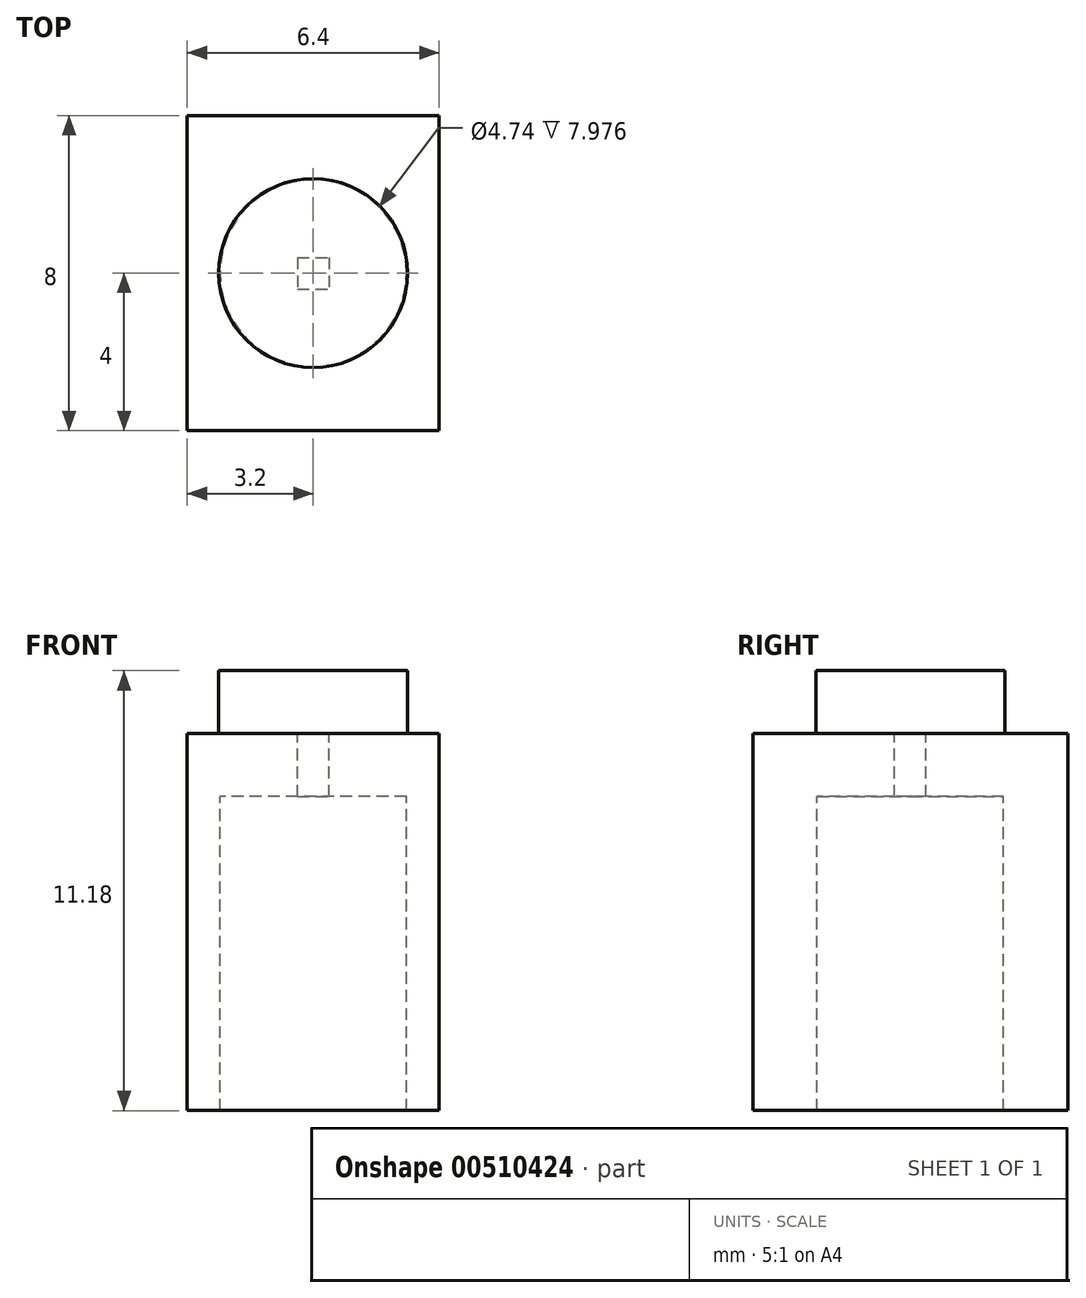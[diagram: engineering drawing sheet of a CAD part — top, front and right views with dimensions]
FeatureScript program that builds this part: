
annotation { "Feature Type Name" : "Feature", "Feature Type Description" : "" }
export const myFeature = defineFeature(function(context is Context, id is Id, definition is map)
    precondition{}
    {
        {
            var Q0;
            Q0=qCreatedBy(makeId("Front.planeOp"),FACE);
            var sketch = newSketch(context, id + "F0", { "sketchPlane" : qUnion([Q0])});
            skLineSegment(sketch, "E0", {"start": v(0, 0) * mm, "end": v(-3.2, 0) * mm});
            skLineSegment(sketch, "E1.MirrorCS", {"start": v(0, 0) * mm, "end": v(3.2, 0) * mm});
            skLineSegment(sketch, "E2", {"start": v(3.2, 0) * mm, "end": v(3.2, -9.58) * mm});
            skLineSegment(sketch, "E3.MirrorCS", {"start": v(-3.2, 0) * mm, "end": v(-3.2, -9.58) * mm});
            skLineSegment(sketch, "E4", {"start": v(-3.2, -9.58) * mm, "end": v(3.2, -9.58) * mm});
            skSolve(sketch);
        }
        {
            var Q0;
            Q0=qCreatedBy(makeId("Top.planeOp"),FACE);
            var sketch = newSketch(context, id + "F1", { "sketchPlane" : qUnion([Q0])});
            skCircle(sketch, "E5", {"center": v(0, 0) * mm, "radius": 2.4 * mm});
            skSolve(sketch);
        }
        {
            var Q0;
            Q0=qCreatedBy(makeId("Top.planeOp"),FACE);
            var sketch = newSketch(context, id + "F2", { "sketchPlane" : qUnion([Q0])});
            skCircle(sketch, "E6", {"center": v(0, 0) * mm, "radius": 2.37 * mm});
            skSolve(sketch);
        }
        {
            var Q0;
            Q0=qCreatedBy(makeId("Top.planeOp"),FACE);
            var sketch = newSketch(context, id + "F3", { "sketchPlane" : qUnion([Q0])});
            skLineSegment(sketch, "E7.bottom", {"start": v(-0.4, 0.4) * mm, "end": v(0.4, 0.4) * mm});
            skLineSegment(sketch, "E7.top", {"start": v(-0.4, -0.4) * mm, "end": v(0.4, -0.4) * mm});
            skLineSegment(sketch, "E7.left", {"start": v(-0.4, 0.4) * mm, "end": v(-0.4, -0.4) * mm});
            skLineSegment(sketch, "E7.right", {"start": v(0.4, 0.4) * mm, "end": v(0.4, -0.4) * mm});
            skPoint(sketch, "E7.middle", {"position": v(0, 0) * mm});
            skSolve(sketch);
        }
        {
            var Q0;
            Q0=makeQuery(id+"F0.imprint","IMPRINT",FACE,{"disambiguationData":[TD([[makeQuery(id+"F0.imprint","IMPRINT",EDGE,{"derivedFrom":sQuery(id+"F0.wireOp",EDGE,"E0")}),1.0]])]});
            extrude(context, id + "F4", {"entities" : qUnion([Q0]), "endBound" : BoundingType.SYMMETRIC, "depth" : 8 * mm});
        }
        {
            var Q0;
            Q0 = qSketchRegion(id + "F1", true);
            extrude(context, id + "F5", {"entities" : qUnion([Q0]), "operationType" : NewBodyOperationType.ADD, "depth" : 1.6 * mm});
        }
        {
            var Q0;
            Q0 = qSketchRegion(id + "F2", true);
            extrude(context, id + "F6", {"entities" : qUnion([Q0]), "operationType" : NewBodyOperationType.REMOVE, "oppositeDirection" : true, "depth" : 25.4 * mm});
        }
        {
            var Q0;
            Q0=makeQuery(id+"F6.boolean.opBoolean","COPY",FACE,{"derivedFrom":makeQuery(id+"F6.opExtrude","CAP_FACE",FACE,{"disambiguationData":[OSD([sQuery(id+"F2.wireOp",EDGE,"E6")])],"isStart":true})});
            extrude(context, id + "F7", {"entities" : qUnion([Q0]), "operationType" : NewBodyOperationType.ADD, "depth" : 1.6 * mm});
        }
        {
            var Q0;
            Q0 = qSketchRegion(id + "F3", true);
            extrude(context, id + "F8", {"entities" : qUnion([Q0]), "operationType" : NewBodyOperationType.REMOVE, "oppositeDirection" : true, "depth" : 1.6 * mm});
        }
    });
